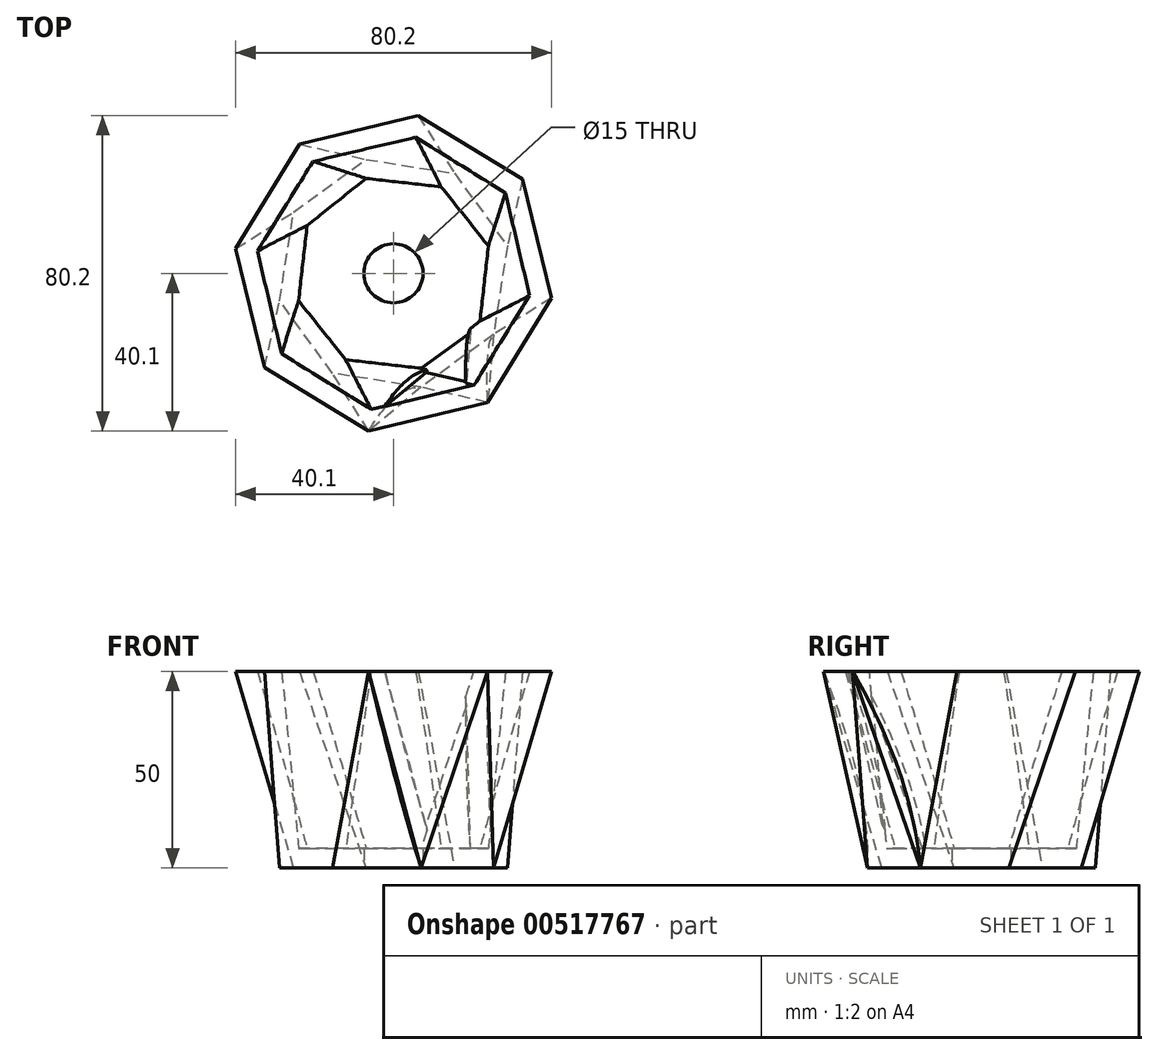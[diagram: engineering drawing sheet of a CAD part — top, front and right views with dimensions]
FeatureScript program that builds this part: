
annotation { "Feature Type Name" : "Feature", "Feature Type Description" : "" }
export const myFeature = defineFeature(function(context is Context, id is Id, definition is map)
    precondition{}
    {
        {
            var Q0;
            Q0=qCreatedBy(makeId("Top.planeOp"),FACE);
            var sketch = newSketch(context, id + "F0", { "sketchPlane" : qUnion([Q0])});
            skCircle(sketch, "E0.cCircle", {"center": v(0, 0) * mm, "radius": 27.5 * mm, "construction": true});
            skLineSegment(sketch, "E0.0", {"start": v(-7, 28.93) * mm, "end": v(15.5, 25.4) * mm});
            skLineSegment(sketch, "E0.1", {"start": v(15.5, 25.4) * mm, "end": v(28.93, 7) * mm});
            skLineSegment(sketch, "E0.2", {"start": v(28.93, 7) * mm, "end": v(25.4, -15.5) * mm});
            skLineSegment(sketch, "E0.3", {"start": v(25.4, -15.5) * mm, "end": v(7, -28.93) * mm});
            skLineSegment(sketch, "E0.4", {"start": v(7, -28.93) * mm, "end": v(-15.5, -25.4) * mm});
            skLineSegment(sketch, "E0.5", {"start": v(-15.5, -25.4) * mm, "end": v(-28.93, -7) * mm});
            skLineSegment(sketch, "E0.6", {"start": v(-28.93, -7) * mm, "end": v(-25.4, 15.5) * mm});
            skLineSegment(sketch, "E0.7", {"start": v(-25.4, 15.5) * mm, "end": v(-7, 28.93) * mm});
            skPoint(sketch, "E0.0.midPoint", {"position": v(4.25, 27.17) * mm});
            skSolve(sketch);
        }
        {
            var Q0;
            Q0=qCreatedBy(makeId("Top.planeOp"),FACE);
            cPlane(context, id + "F1", {"entities" : qUnion([Q0]), "cplaneType" : CPlaneType.OFFSET, "offset" : 50 * mm, "width" : 150 * mm, "height" : 150 * mm});
        }
        {
            var Q0;
            Q0=qCreatedBy(id+"F1.planeOp",FACE);
            var sketch = newSketch(context, id + "F2", { "sketchPlane" : qUnion([Q0])});
            skCircle(sketch, "E1.cCircle", {"center": v(0, 0) * mm, "radius": 37.5 * mm, "construction": true});
            skLineSegment(sketch, "E1.0", {"start": v(6.28, 40.1) * mm, "end": v(32.8, 23.92) * mm});
            skLineSegment(sketch, "E1.1", {"start": v(32.8, 23.92) * mm, "end": v(40.1, -6.28) * mm});
            skLineSegment(sketch, "E1.2", {"start": v(40.1, -6.28) * mm, "end": v(23.92, -32.8) * mm});
            skLineSegment(sketch, "E1.3", {"start": v(23.92, -32.8) * mm, "end": v(-6.28, -40.1) * mm});
            skLineSegment(sketch, "E1.4", {"start": v(-6.28, -40.1) * mm, "end": v(-32.8, -23.92) * mm});
            skLineSegment(sketch, "E1.5", {"start": v(-32.8, -23.92) * mm, "end": v(-40.1, 6.28) * mm});
            skLineSegment(sketch, "E1.6", {"start": v(-40.1, 6.28) * mm, "end": v(-23.92, 32.8) * mm});
            skLineSegment(sketch, "E1.7", {"start": v(-23.92, 32.8) * mm, "end": v(6.28, 40.1) * mm});
            skPoint(sketch, "E1.0.midPoint", {"position": v(19.53, 32.01) * mm});
            skLineSegment(sketch, "E2", {"start": v(-8.82, 36.45) * mm, "end": v(8.82, -36.45) * mm, "construction": true});
            skPoint(sketch, "E3.0", {"position": v(-7, 28.93) * mm});
            skSolve(sketch);
        }
        {
            var Q0;
            Q0=sQuery(id+"F2.wireOp",VERTEX,"E1.4.start");
            var Q1;
            Q1=sQuery(id+"F2.wireOp",VERTEX,"E1.3.start");
            var Q2;
            Q2=sQuery(id+"F0.wireOp",VERTEX,"E0.4.start");
            cPlane(context, id + "F3", {"entities" : qUnion([Q0, Q1, Q2]), "cplaneType" : CPlaneType.THREE_POINT, "offset" : 25 * mm, "width" : 150 * mm, "height" : 150 * mm});
        }
        {
            var Q0;
            Q0=qCreatedBy(id+"F3.planeOp",FACE);
            var sketch = newSketch(context, id + "F4", { "sketchPlane" : qUnion([Q0])});
            skPoint(sketch, "E4.0", {"position": v(-13.48, 55.68) * mm});
            skPoint(sketch, "E5.0", {"position": v(17.56, 54.53) * mm});
            skPoint(sketch, "E6.0", {"position": v(0.17, 4.55) * mm});
            skLineSegment(sketch, "E7", {"start": v(-13.48, 55.68) * mm, "end": v(17.56, 54.53) * mm});
            skLineSegment(sketch, "E8", {"start": v(17.56, 54.53) * mm, "end": v(0.17, 4.55) * mm});
            skLineSegment(sketch, "E9", {"start": v(0.17, 4.55) * mm, "end": v(-13.48, 55.68) * mm});
            skSolve(sketch);
        }
        {
            var Q0;
            Q0=sQuery(id+"F4.wireOp",VERTEX,"E5.0");
            var Q1;
            Q1=sQuery(id+"F4.wireOp",VERTEX,"E6.0");
            var Q2;
            Q2=sQuery(id+"F0.wireOp",VERTEX,"E0.3.start");
            cPlane(context, id + "F5", {"entities" : qUnion([Q0, Q1, Q2]), "cplaneType" : CPlaneType.THREE_POINT, "offset" : 25 * mm, "width" : 150 * mm, "height" : 150 * mm});
        }
        {
            var Q0;
            Q0=qCreatedBy(id+"F5.planeOp",FACE);
            var sketch = newSketch(context, id + "F6", { "sketchPlane" : qUnion([Q0])});
            skPoint(sketch, "E10.0", {"position": v(-10.65, 57.67) * mm});
            skPoint(sketch, "E11.0", {"position": v(9.94, 8.92) * mm});
            skPoint(sketch, "E12.0", {"position": v(-12.47, 4.78) * mm});
            skLineSegment(sketch, "E13", {"start": v(-10.65, 57.67) * mm, "end": v(9.94, 8.92) * mm});
            skLineSegment(sketch, "E14", {"start": v(9.94, 8.92) * mm, "end": v(-12.47, 4.78) * mm});
            skLineSegment(sketch, "E15", {"start": v(-12.47, 4.78) * mm, "end": v(-10.65, 57.67) * mm});
            skSolve(sketch);
        }
        {
            var Q0;
            Q0=makeQuery(id+"F2.imprint","IMPRINT",FACE,{"disambiguationData":[TD([[makeQuery(id+"F2.imprint","IMPRINT",EDGE,{"derivedFrom":sQuery(id+"F2.wireOp",EDGE,"E1.0")}),-1.0]])]});
            var Q1;
            Q1=makeQuery(id+"F0.imprint","IMPRINT",FACE,{"disambiguationData":[TD([[makeQuery(id+"F0.imprint","IMPRINT",EDGE,{"derivedFrom":sQuery(id+"F0.wireOp",EDGE,"E0.0")}),-1.0]])]});
            loft(context, id + "F7", {"sheetProfilesArray" : [{ "sheetProfileEntities" : qUnion([Q0]) }, { "sheetProfileEntities" : qUnion([Q1]) }]});
        }
        {
            var Q0;
            Q0 = qSketchRegion(id + "F4", true);
            var Q1;
            Q1 = qSketchRegion(id + "F6", true);
            var Q2;
            Q2=makeQuery(id+"F7.opLoft","SWEPT_BODY",BODY,{"disambiguationData":[OSD([makeQuery(id+"F0.imprint","IMPRINT",FACE,{"disambiguationData":[TD([[makeQuery(id+"F0.imprint","IMPRINT",EDGE,{"derivedFrom":sQuery(id+"F0.wireOp",EDGE,"E0.0")}),-1.0]])]}),makeQuery(id+"F2.imprint","IMPRINT",FACE,{"disambiguationData":[TD([[makeQuery(id+"F2.imprint","IMPRINT",EDGE,{"derivedFrom":sQuery(id+"F2.wireOp",EDGE,"E1.0")}),-1.0]])]})])]});
            extrude(context, id + "F8", {"entities" : qUnion([Q0, Q1]), "operationType" : NewBodyOperationType.ADD, "endBound" : BoundingType.UP_TO_BODY, "oppositeDirection" : true, "depth" : 25 * mm, "endBoundEntityBody" : qUnion([Q2]), "offsetDistance" : 25 * mm});
        }
        {
            var Q0;
            Q0=makeQuery(id+"F7.opLoft","CAP_FACE",FACE,{"disambiguationData":[OSD([makeQuery(id+"F2.imprint","IMPRINT",FACE,{"disambiguationData":[TD([[makeQuery(id+"F2.imprint","IMPRINT",EDGE,{"derivedFrom":sQuery(id+"F2.wireOp",EDGE,"E1.0")}),-1.0]])]})])],"isStart":true});
            shell(context, id + "F9", {"entities" : qUnion([Q0]), "thickness" : 5 * mm});
        }
        {
            var Q0;
            Q0=sQuery(id+"F0.wireOp",VERTEX,"E0.cCircle.center");
            var Q1;
            Q1=makeQuery(id+"F7.opLoft","SWEPT_BODY",BODY,{"disambiguationData":[OSD([makeQuery(id+"F0.imprint","IMPRINT",FACE,{"disambiguationData":[TD([[makeQuery(id+"F0.imprint","IMPRINT",EDGE,{"derivedFrom":sQuery(id+"F0.wireOp",EDGE,"E0.0")}),-1.0]])]}),makeQuery(id+"F2.imprint","IMPRINT",FACE,{"disambiguationData":[TD([[makeQuery(id+"F2.imprint","IMPRINT",EDGE,{"derivedFrom":sQuery(id+"F2.wireOp",EDGE,"E1.0")}),-1.0]])]})])]});
            hole(context, id + "F10", {"style" : HoleStyle.SIMPLE, "endStyle" : HoleEndStyle.THROUGH, "oppositeDirection" : true, "holeDiameter" : 15 * mm, "isTappedThrough" : true, "tappedDepth" : 12 * mm, "tapClearance" : 3, "startFromSketch" : true, "locations" : qUnion([Q0]), "scope" : qUnion([Q1])});
        }
    });
